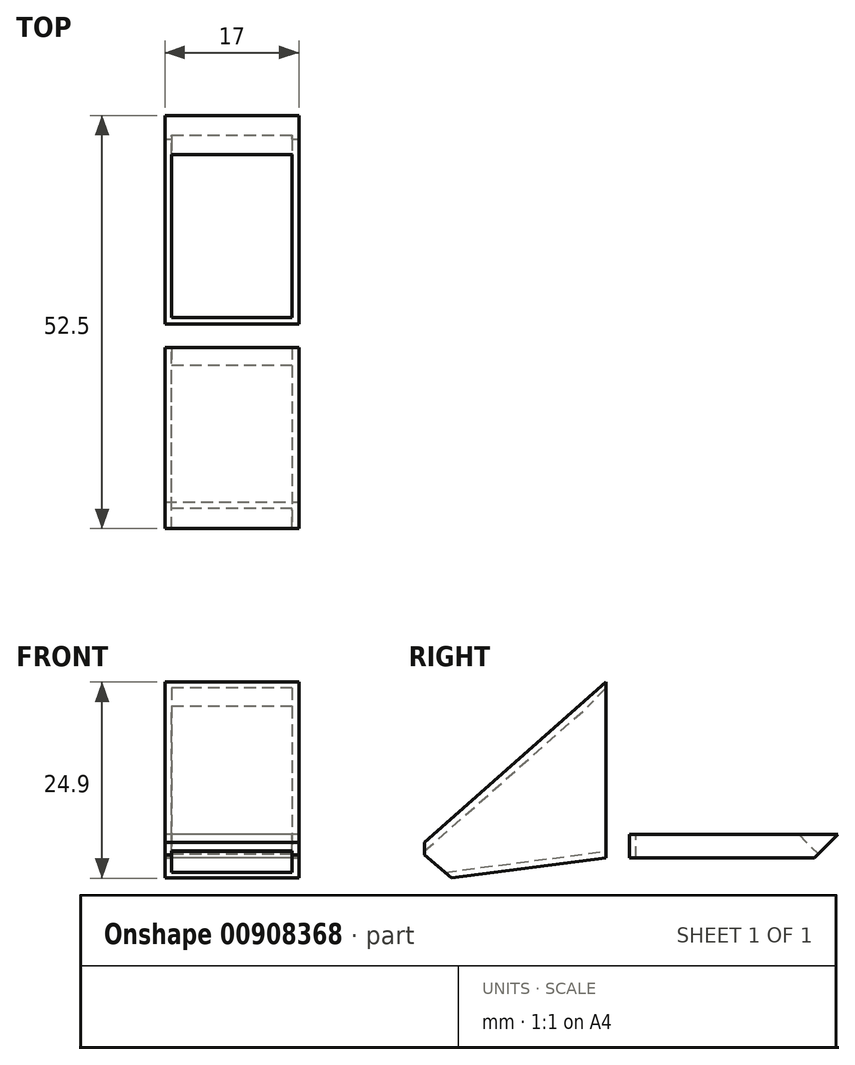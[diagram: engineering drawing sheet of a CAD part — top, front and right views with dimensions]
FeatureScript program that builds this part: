
annotation { "Feature Type Name" : "Feature", "Feature Type Description" : "" }
export const myFeature = defineFeature(function(context is Context, id is Id, definition is map)
    precondition{}
    {
        {
            var Q0;
            Q0=qCreatedBy(makeId("Front.planeOp"),FACE);
            var sketch = newSketch(context, id + "F0", { "sketchPlane" : qUnion([Q0])});
            skLineSegment(sketch, "E0.bottom", {"start": v(8.5, 10.75) * mm, "end": v(-8.5, 10.75) * mm});
            skLineSegment(sketch, "E0.top", {"start": v(8.5, -10.75) * mm, "end": v(-8.5, -10.75) * mm});
            skLineSegment(sketch, "E0.left", {"start": v(8.5, 10.75) * mm, "end": v(8.5, -10.75) * mm});
            skLineSegment(sketch, "E0.right", {"start": v(-8.5, 10.75) * mm, "end": v(-8.5, -10.75) * mm});
            skPoint(sketch, "E0.middle", {"position": v(0, 0) * mm});
            skLineSegment(sketch, "E1.0", {"start": v(7.66, 10.75) * mm, "end": v(7.66, -9.9) * mm});
            skLineSegment(sketch, "E1.1", {"start": v(7.66, -9.9) * mm, "end": v(-7.66, -9.9) * mm});
            skLineSegment(sketch, "E1.2", {"start": v(-7.66, 10.75) * mm, "end": v(-7.66, -9.9) * mm});
            skSolve(sketch);
        }
        {
            var Q0;
            Q0=makeQuery(id+"F0.imprint","IMPRINT",FACE,{"disambiguationData":[TD([[makeQuery(id+"F0.imprint","IMPRINT",EDGE,{"derivedFrom":sQuery(id+"F0.wireOp",EDGE,"E0.top")}),-1.0]])]});
            extrude(context, id + "F1", {"entities" : qUnion([Q0]), "oppositeDirection" : true, "depth" : 3 * mm, "offsetDistance" : 25 * mm});
        }
        {
            var Q0;
            Q0=makeQuery(id+"F1.opExtrude","CAP_FACE",FACE,{"disambiguationData":[OSD([sQuery(id+"F0.wireOp",EDGE,"E0.bottom"),sQuery(id+"F0.wireOp",EDGE,"E0.top"),sQuery(id+"F0.wireOp",EDGE,"E0.left"),sQuery(id+"F0.wireOp",EDGE,"E0.right"),sQuery(id+"F0.wireOp",EDGE,"E1.0"),sQuery(id+"F0.wireOp",EDGE,"E1.1"),sQuery(id+"F0.wireOp",EDGE,"E1.2")])],"isStart":false});
            var sketch = newSketch(context, id + "F2", { "sketchPlane" : qUnion([Q0])});
            skLineSegment(sketch, "E2.bottom", {"start": v(8.5, 10.75) * mm, "end": v(-8.5, 10.75) * mm});
            skLineSegment(sketch, "E2.top", {"start": v(8.5, 15.75) * mm, "end": v(-8.5, 15.75) * mm});
            skLineSegment(sketch, "E2.left", {"start": v(8.5, 10.75) * mm, "end": v(8.5, 15.75) * mm});
            skLineSegment(sketch, "E2.right", {"start": v(-8.5, 10.75) * mm, "end": v(-8.5, 15.75) * mm});
            skSolve(sketch);
        }
        {
            var Q0;
            Q0=makeQuery(id+"F2.imprint","IMPRINT",FACE,{"disambiguationData":[TD([[makeQuery(id+"F2.imprint","IMPRINT",EDGE,{"derivedFrom":sQuery(id+"F2.wireOp",EDGE,"E2.top")}),1.0]])]});
            var Q1;
            Q1=makeQuery(id+"F1.opExtrude","CAP_FACE",FACE,{"disambiguationData":[OSD([sQuery(id+"F0.wireOp",EDGE,"E0.bottom"),sQuery(id+"F0.wireOp",EDGE,"E0.top"),sQuery(id+"F0.wireOp",EDGE,"E0.left"),sQuery(id+"F0.wireOp",EDGE,"E0.right"),sQuery(id+"F0.wireOp",EDGE,"E1.0"),sQuery(id+"F0.wireOp",EDGE,"E1.1"),sQuery(id+"F0.wireOp",EDGE,"E1.2")])],"isStart":true});
            extrude(context, id + "F3", {"entities" : qUnion([Q0]), "operationType" : NewBodyOperationType.ADD, "endBound" : BoundingType.UP_TO_SURFACE, "oppositeDirection" : true, "depth" : 25 * mm, "endBoundEntityFace" : qUnion([Q1]), "offsetDistance" : 25 * mm});
        }
        {
            var Q0;
            Q0=makeQuery(id+"F3.opExtrude","CAP_EDGE",EDGE,{"disambiguationData":[OSD([sQuery(id+"F2.wireOp",EDGE,"E2.top")])],"isStart":true});
            chamfer(context, id + "F4", {"entities" : qUnion([Q0]), "width" : 3 * mm, "tangentPropagation" : true});
        }
        {
            var Q0;
            Q0=makeQuery(id+"F3.opExtrude","CAP_EDGE",EDGE,{"disambiguationData":[OSD([sQuery(id+"F2.wireOp",EDGE,"E2.bottom")])],"isStart":true});
            chamfer(context, id + "F5", {"entities" : qUnion([Q0]), "width" : 3 * mm, "tangentPropagation" : true});
        }
        {
            var Q0;
            Q0=makeQuery(id+"F3.boolean.opBoolean","MERGE",FACE,{"derivedFrom":[makeQuery(id+"F1.opExtrude","CAP_FACE",FACE,{"disambiguationData":[OSD([sQuery(id+"F0.wireOp",EDGE,"E0.bottom"),sQuery(id+"F0.wireOp",EDGE,"E0.top"),sQuery(id+"F0.wireOp",EDGE,"E0.left"),sQuery(id+"F0.wireOp",EDGE,"E0.right"),sQuery(id+"F0.wireOp",EDGE,"E1.0"),sQuery(id+"F0.wireOp",EDGE,"E1.1"),sQuery(id+"F0.wireOp",EDGE,"E1.2")])],"isStart":true}),makeQuery(id+"F3.opExtrude","CAP_FACE",FACE,{"disambiguationData":[OSD([sQuery(id+"F2.wireOp",EDGE,"E2.bottom"),sQuery(id+"F2.wireOp",EDGE,"E2.top"),sQuery(id+"F2.wireOp",EDGE,"E2.left"),sQuery(id+"F2.wireOp",EDGE,"E2.right")])],"isStart":false})]});
            var sketch = newSketch(context, id + "F6", { "sketchPlane" : qUnion([Q0])});
            skLineSegment(sketch, "E3.bottom", {"start": v(-8.5, 11.6) * mm, "end": v(8.5, 11.6) * mm});
            skLineSegment(sketch, "E3.top", {"start": v(-8.5, -10.75) * mm, "end": v(8.5, -10.75) * mm});
            skLineSegment(sketch, "E3.left", {"start": v(-8.5, 11.6) * mm, "end": v(-8.5, -10.75) * mm});
            skLineSegment(sketch, "E3.right", {"start": v(8.5, 11.6) * mm, "end": v(8.5, -10.75) * mm});
            skSolve(sketch);
        }
        {
            var Q0;
            Q0=qCreatedBy(makeId("Front.planeOp"),FACE);
            cPlane(context, id + "F7", {"entities" : qUnion([Q0]), "cplaneType" : CPlaneType.OFFSET, "offset" : 23 * mm, "width" : 150 * mm, "height" : 150 * mm});
        }
        {
            var Q0;
            Q0=qCreatedBy(id+"F7.planeOp",FACE);
            var sketch = newSketch(context, id + "F8", { "sketchPlane" : qUnion([Q0])});
            skLineSegment(sketch, "E4.bottom", {"start": v(-8.5, -13.75) * mm, "end": v(8.5, -13.75) * mm});
            skLineSegment(sketch, "E4.top", {"start": v(-8.5, -8.75) * mm, "end": v(8.5, -8.75) * mm});
            skLineSegment(sketch, "E4.left", {"start": v(-8.5, -13.75) * mm, "end": v(-8.5, -8.75) * mm});
            skLineSegment(sketch, "E4.right", {"start": v(8.5, -13.75) * mm, "end": v(8.5, -8.75) * mm});
            skSolve(sketch);
        }
        {
            var Q1;
            Q1 = qSketchRegion(id + "F6", true);
            var Q2;
            Q2 = qSketchRegion(id + "F8", true);
            loft(context, id + "F9", {"sheetProfilesArray" : [{ "sheetProfileEntities" : qUnion([Q1]) }, { "sheetProfileEntities" : qUnion([Q2]) }]});
        }
        {
            var Q0;
            Q0=makeQuery(id+"F9.opLoft","CAP_FACE",FACE,{"disambiguationData":[OSD([makeQuery(id+"F6.imprint","IMPRINT",FACE,{"disambiguationData":[TD([[makeQuery(id+"F6.imprint","IMPRINT",EDGE,{"derivedFrom":sQuery(id+"F6.wireOp",EDGE,"E3.bottom")}),-1.0]])]})])],"isStart":true});
            var Q1;
            Q1=makeQuery(id+"F9.opLoft","CAP_FACE",FACE,{"disambiguationData":[OSD([makeQuery(id+"F8.imprint","IMPRINT",FACE,{"disambiguationData":[TD([[makeQuery(id+"F8.imprint","IMPRINT",EDGE,{"derivedFrom":sQuery(id+"F8.wireOp",EDGE,"E4.bottom")}),1.0]])]})])],"isStart":true});
            shell(context, id + "F10", {"entities" : qUnion([Q0, Q1]), "thickness" : 0.84 * mm});
        }
        {
            var Q0;
            Q0=makeQuery(id+"F9.opLoft","MID_CAP_EDGE",EDGE,{"disambiguationData":[OSD([sQuery(id+"F8.wireOp",EDGE,"E4.bottom"),sQuery(id+"F8.wireOp",EDGE,"E4.left"),sQuery(id+"F8.wireOp",EDGE,"E4.right")])],"capPos":1.0});
            chamfer(context, id + "F11", {"entities" : qUnion([Q0]), "width" : 3 * mm, "tangentPropagation" : true});
        }
        {
            var Q0;
            Q0=makeQuery(id+"F10.opShell","OFFSET_EDGE",EDGE,{"disambiguationData":[OSD([sQuery(id+"F0.wireOp",EDGE,"E0.left"),sQuery(id+"F0.wireOp",EDGE,"E0.right"),sQuery(id+"F2.wireOp",EDGE,"E2.left"),sQuery(id+"F2.wireOp",EDGE,"E2.right"),sQuery(id+"F6.wireOp",EDGE,"E3.bottom"),sQuery(id+"F6.wireOp",EDGE,"E3.left"),sQuery(id+"F6.wireOp",EDGE,"E3.right")])]});
            chamfer(context, id + "F12", {"entities" : qUnion([Q0]), "chamferType" : ChamferType.OFFSET_ANGLE, "width" : 3 * mm, "oppositeDirection" : true, "angle" : 5 * degree, "tangentPropagation" : true});
        }
        {
            var Q0;
            Q0=makeQuery(id+"F1.opExtrude","SWEPT_BODY",BODY,{"disambiguationData":[OSD([sQuery(id+"F0.wireOp",EDGE,"E0.bottom"),sQuery(id+"F0.wireOp",EDGE,"E0.top"),sQuery(id+"F0.wireOp",EDGE,"E0.left"),sQuery(id+"F0.wireOp",EDGE,"E0.right"),sQuery(id+"F0.wireOp",EDGE,"E1.0"),sQuery(id+"F0.wireOp",EDGE,"E1.1"),sQuery(id+"F0.wireOp",EDGE,"E1.2")])]});
            var Q1;
            Q1=makeQuery(id+"F1.opExtrude","CAP_EDGE",EDGE,{"disambiguationData":[OSD([sQuery(id+"F0.wireOp",EDGE,"E0.top")])],"isStart":false});
            transform(context, id + "F13", {"entities" : qUnion([Q0]), "transformType" : TransformType.ROTATION, "transformAxis" : qUnion([Q1]), "angle" : 90 * degree, "makeCopy" : false});
        }
    });
